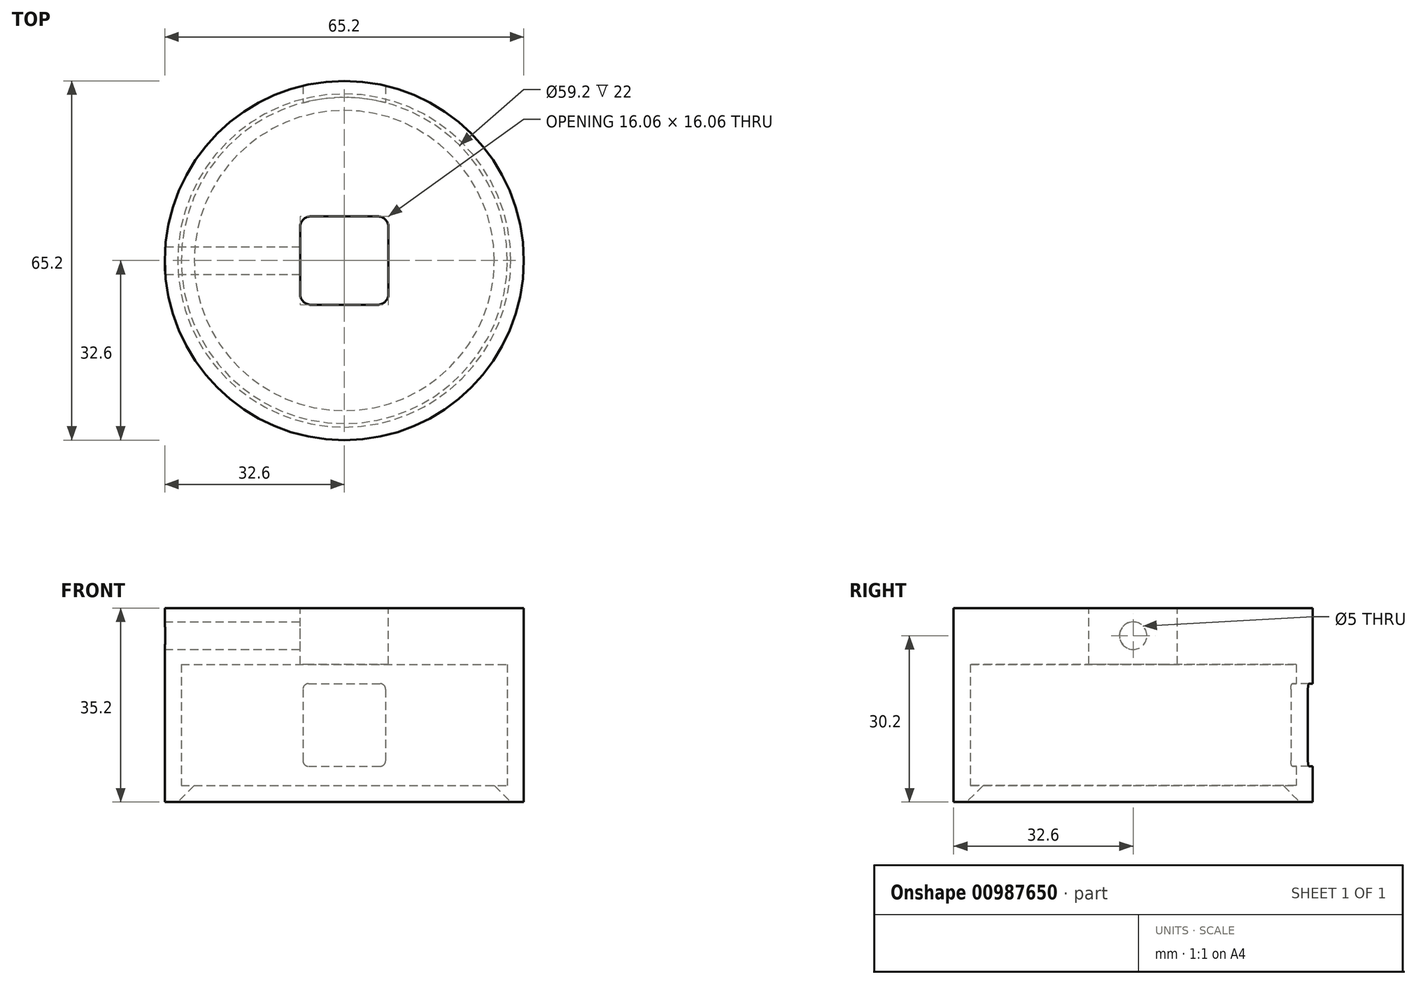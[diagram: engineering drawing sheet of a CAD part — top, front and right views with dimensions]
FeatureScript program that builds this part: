
annotation { "Feature Type Name" : "Feature", "Feature Type Description" : "" }
export const myFeature = defineFeature(function(context is Context, id is Id, definition is map)
    precondition{}
    {
        {
            var Q0;
            Q0=qCreatedBy(makeId("Front.planeOp"),FACE);
            var sketch = newSketch(context, id + "F0", { "sketchPlane" : qUnion([Q0])});
            skLineSegment(sketch, "E0", {"start": v(0, 0) * mm, "end": v(-32.6, 0) * mm});
            skLineSegment(sketch, "E1", {"start": v(-32.6, 0) * mm, "end": v(-32.6, -35.2) * mm});
            skLineSegment(sketch, "E2", {"start": v(-32.6, -35.2) * mm, "end": v(-30.25, -35.2) * mm});
            skLineSegment(sketch, "E3", {"start": v(-30.25, -35.2) * mm, "end": v(-27.25, -32.2) * mm});
            skLineSegment(sketch, "E4", {"start": v(-27.25, -32.2) * mm, "end": v(-29.6, -32.2) * mm});
            skLineSegment(sketch, "E5", {"start": v(-29.6, -32.2) * mm, "end": v(-29.6, -10.2) * mm});
            skLineSegment(sketch, "E6", {"start": v(-29.6, -10.2) * mm, "end": v(0, -10.2) * mm});
            skLineSegment(sketch, "E7", {"start": v(0, -10.2) * mm, "end": v(0, 0) * mm});
            skSolve(sketch);
        }
        {
            var Q0;
            Q0=makeQuery(id+"F0.imprint","IMPRINT",FACE,{"disambiguationData":[TD([[makeQuery(id+"F0.imprint","IMPRINT",EDGE,{"derivedFrom":sQuery(id+"F0.wireOp",EDGE,"E0")}),1.0]])]});
            var Q1;
            Q1=sQuery(id+"F0.wireOp",EDGE,"E7");
            revolve(context, id + "F1", {"surfaceOperationType" : NewSurfaceOperationType.NEW, "entities" : qUnion([Q0]), "axis" : qUnion([Q1]), "revolveType" : RevolveType.FULL});
        }
        {
            var Q0;
            Q0=makeQuery(id+"F1.opRevolve","SWEPT_FACE",FACE,{"disambiguationData":[OSD([sQuery(id+"F0.wireOp",EDGE,"E0")])]});
            var sketch = newSketch(context, id + "F2", { "sketchPlane" : qUnion([Q0])});
            skLineSegment(sketch, "E8.bottom", {"start": v(6.03, 8.03) * mm, "end": v(-6.03, 8.03) * mm});
            skLineSegment(sketch, "E8.top", {"start": v(6.03, -8.03) * mm, "end": v(-6.03, -8.03) * mm});
            skLineSegment(sketch, "E8.left", {"start": v(8.03, 6.03) * mm, "end": v(8.03, -6.03) * mm});
            skLineSegment(sketch, "E8.right", {"start": v(-8.03, 6.03) * mm, "end": v(-8.03, -6.03) * mm});
            skPoint(sketch, "E8.middle", {"position": v(0, 0) * mm});
            skPoint(sketch, "E9.visualSharp", {"position": v(-8.03, 8.03) * mm});
            skArc(sketch, "E9.filletArc", {"start": v(-6.03, 8.03) * mm, "mid": v(-7.44, 7.44) * mm, "end": v(-8.03, 6.03) * mm});
            skPoint(sketch, "E10.visualSharp", {"position": v(8.03, 8.03) * mm});
            skArc(sketch, "E10.filletArc", {"start": v(8.03, 6.03) * mm, "mid": v(7.44, 7.44) * mm, "end": v(6.03, 8.03) * mm});
            skPoint(sketch, "E11.visualSharp", {"position": v(8.03, -8.03) * mm});
            skArc(sketch, "E11.filletArc", {"start": v(6.03, -8.03) * mm, "mid": v(7.44, -7.44) * mm, "end": v(8.03, -6.03) * mm});
            skPoint(sketch, "E12.visualSharp", {"position": v(-8.03, -8.03) * mm});
            skArc(sketch, "E12.filletArc", {"start": v(-8.03, -6.03) * mm, "mid": v(-7.44, -7.44) * mm, "end": v(-6.03, -8.03) * mm});
            skSolve(sketch);
        }
        {
            var Q0;
            Q0=qSketchRegion(id+"F2",true);
            extrude(context, id + "F3", {"entities" : qUnion([Q0]), "operationType" : NewBodyOperationType.REMOVE, "oppositeDirection" : true, "depth" : 25 * mm, "offsetDistance" : 25 * mm});
        }
        {
            var Q0;
            Q0=makeQuery(id+"F3.boolean.opBoolean","COPY",FACE,{"derivedFrom":makeQuery(id+"F3.opExtrude","SWEPT_FACE",FACE,{"disambiguationData":[OSD([sQuery(id+"F2.wireOp",EDGE,"E8.right")])]})});
            var sketch = newSketch(context, id + "F4", { "sketchPlane" : qUnion([Q0])});
            skCircle(sketch, "E13", {"center": v(0, -5) * mm, "radius": 2.5 * mm});
            skSolve(sketch);
        }
        {
            var Q0;
            Q0=qSketchRegion(id+"F4",true);
            extrude(context, id + "F5", {"entities" : qUnion([Q0]), "operationType" : NewBodyOperationType.REMOVE, "endBound" : BoundingType.THROUGH_ALL, "oppositeDirection" : true, "depth" : 25 * mm, "offsetDistance" : 25 * mm});
        }
        {
            var Q0;
            Q0=qCreatedBy(makeId("Front.planeOp"),FACE);
            var sketch = newSketch(context, id + "F6", { "sketchPlane" : qUnion([Q0])});
            skLineSegment(sketch, "E14.bottom", {"start": v(-6.5, -28.7) * mm, "end": v(6.5, -28.7) * mm});
            skLineSegment(sketch, "E14.top", {"start": v(-6.5, -13.7) * mm, "end": v(6.5, -13.7) * mm});
            skLineSegment(sketch, "E14.left", {"start": v(-7.5, -27.7) * mm, "end": v(-7.5, -14.7) * mm});
            skLineSegment(sketch, "E14.right", {"start": v(7.5, -27.7) * mm, "end": v(7.5, -14.7) * mm});
            skPoint(sketch, "E15.visualSharp", {"position": v(-7.5, -13.7) * mm});
            skArc(sketch, "E15.filletArc", {"start": v(-6.5, -13.7) * mm, "mid": v(-7.2, -14) * mm, "end": v(-7.5, -14.7) * mm});
            skPoint(sketch, "E16.visualSharp", {"position": v(7.5, -13.7) * mm});
            skArc(sketch, "E16.filletArc", {"start": v(7.5, -14.7) * mm, "mid": v(7.2, -14) * mm, "end": v(6.5, -13.7) * mm});
            skPoint(sketch, "E17.visualSharp", {"position": v(-7.5, -28.7) * mm});
            skArc(sketch, "E17.filletArc", {"start": v(-7.5, -27.7) * mm, "mid": v(-7.2, -28.4) * mm, "end": v(-6.5, -28.7) * mm});
            skPoint(sketch, "E18.visualSharp", {"position": v(7.5, -28.7) * mm});
            skArc(sketch, "E18.filletArc", {"start": v(6.5, -28.7) * mm, "mid": v(7.2, -28.4) * mm, "end": v(7.5, -27.7) * mm});
            skSolve(sketch);
        }
        {
            var Q0;
            Q0 = qSketchRegion(id + "F6", true);
            extrude(context, id + "F7", {"entities" : qUnion([Q0]), "operationType" : NewBodyOperationType.REMOVE, "endBound" : BoundingType.THROUGH_ALL, "oppositeDirection" : true, "depth" : 25 * mm, "offsetDistance" : 25 * mm});
        }
    });
